# Revit family: Kabelrinne MKS Magic-MKSM Kabelrinne 1 mm, FT,FS
name_source: partatom
category: Generic Models
revit_build: Autodesk Revit 2017 (Build: 20190508_0315(x64)
units: mm (PartAtom-declared; Revit-internal decimal feet)

## family parameters
Always vertical = Yes
Can host rebar = No
Cut with Voids When Loaded = No
Part Type = Normal
Room Calculation Point = No
Round Connector Dimension = Use Diameter
Shared = No
Work Plane-Based = No

## types (2) — shared parameters
Cut's number = 2
Cut's number 2 = 57
Cut's number 3 = 58
Cut's number 4 = 28
Cut's number 5 = 27
Cut's space = 51 mm
Cut's space 2 = 102 mm
Height = 60 mm  [stored 0.19685 ft]
Height 1 = 48 mm  [stored 0.15748 ft]
Length = 3050 mm  [stored 10.0066 ft]
Length 1 = 3000 mm  [stored 9.84252 ft]
Length 2 = 2898 mm
Length 3 = 2949 mm
Length 4 = 2847 mm
Manufacturer = OBO Bettermann
URL = http://www.obo-bettermann.com
Width = 100 mm  [stored 0.328084 ft]
Width 1 = 50 mm  [stored 0.164042 ft]
Width 2 = 50 mm  [stored 0.164042 ft]

## per-type parameters (varying)
| type | GTIN | Manufacturer Art.No. | Material |
| MKSM 610 FT | 4012195830023 | 6059018 | Hot-dip galvanised |
| MKSM 610 FS | 4012195829553 | 6059000 | Strip-galvanised |

note: column(s) folded — value = type name in every type: Article Type

note: [stored X ft] marks values corroborated as IEEE doubles in the binary element streams (Revit-internal decimal feet)

## geometry (parser evidence)
native form markers: Sweep x3
no freeform markers — native parametric forms only
